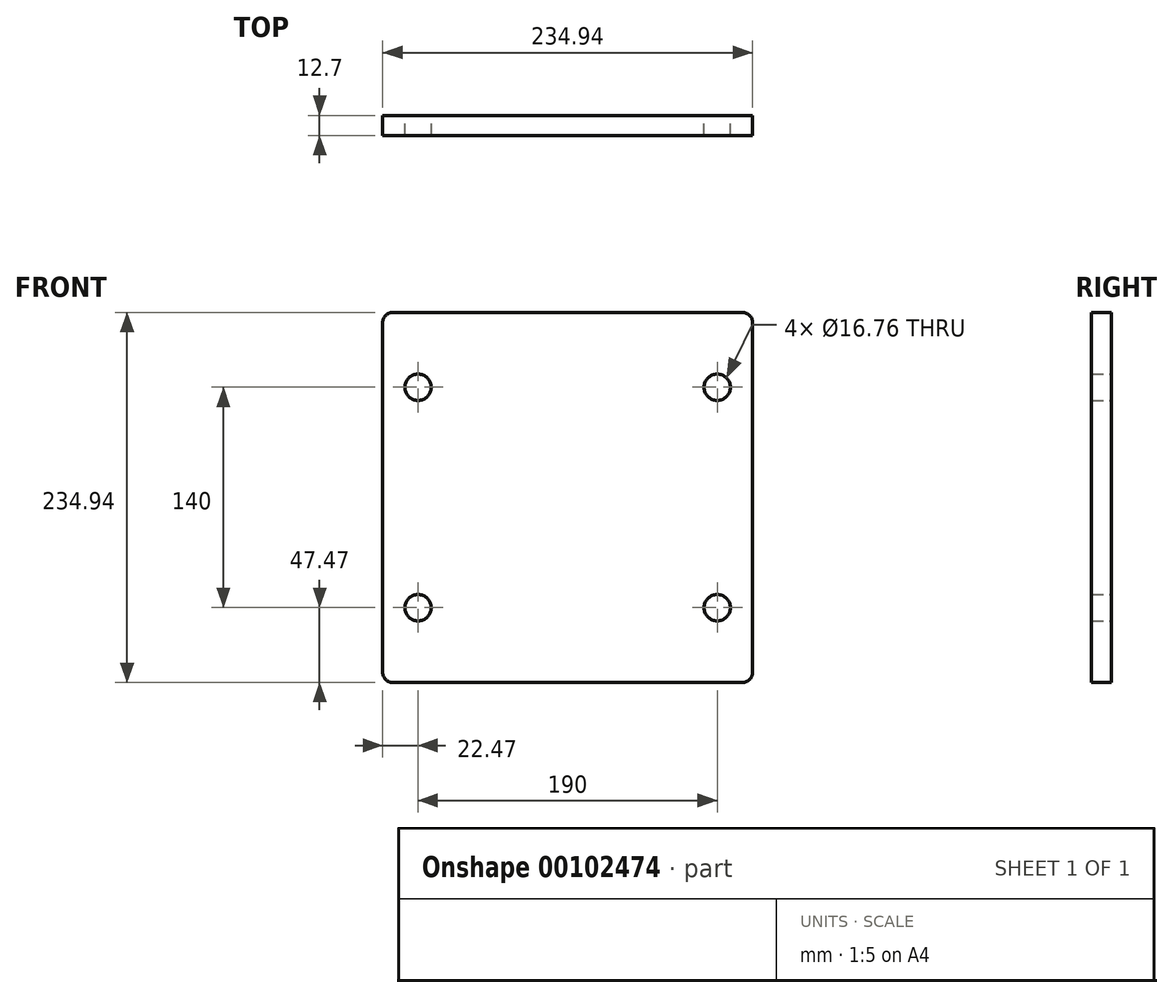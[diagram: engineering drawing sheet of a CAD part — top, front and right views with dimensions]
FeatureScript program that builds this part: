
annotation { "Feature Type Name" : "Feature", "Feature Type Description" : "" }
export const myFeature = defineFeature(function(context is Context, id is Id, definition is map)
    precondition{}
    {
        {
            var Q0;
            Q0=qCreatedBy(makeId("Front.planeOp"),FACE);
            var sketch = newSketch(context, id + "F0", { "sketchPlane" : qUnion([Q0])});
            skLineSegment(sketch, "E0", {"start": v(-111.13, -117.48) * mm, "end": v(111.13, -117.48) * mm});
            skArc(sketch, "E1", {"start": v(111.13, -117.48) * mm, "mid": v(115.62, -115.62) * mm, "end": v(117.48, -111.13) * mm});
            skLineSegment(sketch, "E2", {"start": v(117.48, -111.13) * mm, "end": v(117.48, 111.13) * mm});
            skArc(sketch, "E3", {"start": v(117.48, 111.13) * mm, "mid": v(115.62, 115.62) * mm, "end": v(111.13, 117.48) * mm});
            skLineSegment(sketch, "E4", {"start": v(111.13, 117.48) * mm, "end": v(-111.13, 117.48) * mm});
            skArc(sketch, "E5", {"start": v(-111.13, 117.48) * mm, "mid": v(-115.62, 115.62) * mm, "end": v(-117.48, 111.13) * mm});
            skLineSegment(sketch, "E6", {"start": v(-117.48, 111.13) * mm, "end": v(-117.48, -111.13) * mm});
            skArc(sketch, "E7", {"start": v(-117.48, -111.13) * mm, "mid": v(-115.62, -115.62) * mm, "end": v(-111.13, -117.48) * mm});
            skCircle(sketch, "E8", {"center": v(95, 70) * mm, "radius": 8.38 * mm});
            skCircle(sketch, "E9", {"center": v(-95, 70) * mm, "radius": 8.38 * mm});
            skCircle(sketch, "E10", {"center": v(-95, -70) * mm, "radius": 8.38 * mm});
            skCircle(sketch, "E11", {"center": v(95, -70) * mm, "radius": 8.38 * mm});
            skSolve(sketch);
        }
        {
            var Q0;
            Q0 = qSketchRegion(id + "F0", true);
            extrude(context, id + "F1", {"entities" : qUnion([Q0]), "depth" : 12.7 * mm});
        }
    });
